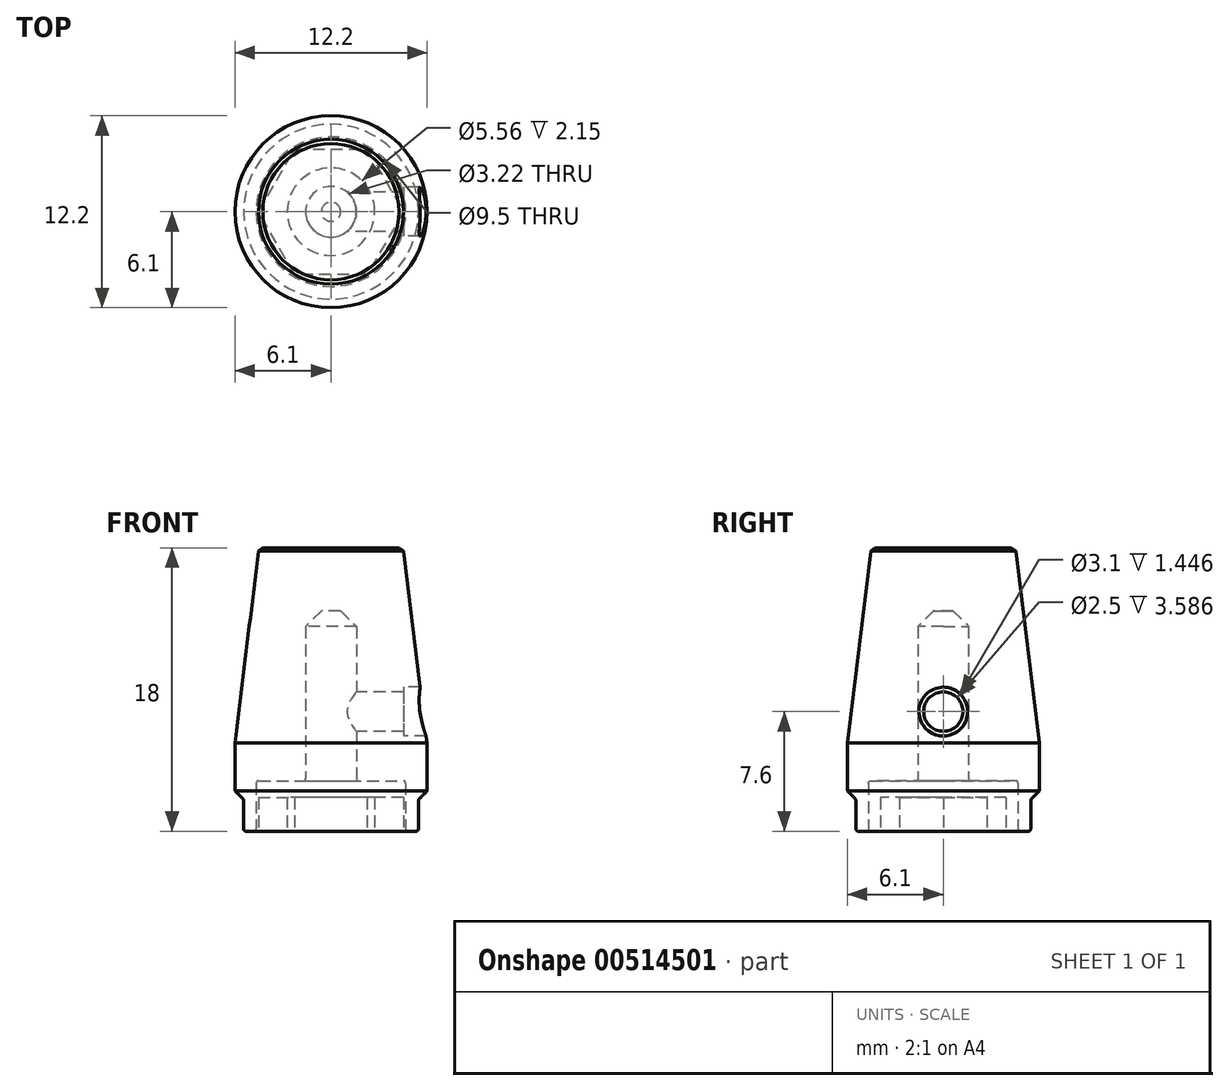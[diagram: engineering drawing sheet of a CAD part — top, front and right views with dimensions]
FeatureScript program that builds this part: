
annotation { "Feature Type Name" : "Feature", "Feature Type Description" : "" }
export const myFeature = defineFeature(function(context is Context, id is Id, definition is map)
    precondition{}
    {
        {
            var Q0;
            Q0=qCreatedBy(makeId("Front.planeOp"),FACE);
            var sketch = newSketch(context, id + "F0", { "sketchPlane" : qUnion([Q0])});
            skLineSegment(sketch, "E0.bottom", {"start": v(4.75, 0) * mm, "end": v(5.55, 0) * mm});
            skLineSegment(sketch, "E0.top", {"start": v(0, 18) * mm, "end": v(4.58, 18) * mm});
            skLineSegment(sketch, "E0.left", {"start": v(0, 3.2) * mm, "end": v(0, 18) * mm, "construction": true});
            skLineSegment(sketch, "E0.right", {"start": v(6.1, 2) * mm, "end": v(6.1, 5.6) * mm});
            skLineSegment(sketch, "E1", {"start": v(1.6, 3.2) * mm, "end": v(4.75, 3.2) * mm});
            skLineSegment(sketch, "E2", {"start": v(4.75, 3.2) * mm, "end": v(4.75, 0) * mm});
            skLineSegment(sketch, "E3", {"start": v(5.55, 0) * mm, "end": v(5.55, 2) * mm});
            skLineSegment(sketch, "E4", {"start": v(5.55, 2) * mm, "end": v(6.1, 2) * mm});
            skLineSegment(sketch, "E5", {"start": v(1.6, 3.2) * mm, "end": v(1.6, 14) * mm});
            skLineSegment(sketch, "E6", {"start": v(1.6, 14) * mm, "end": v(0, 14) * mm});
            skLineSegment(sketch, "E7", {"start": v(0, 18) * mm, "end": v(0, 14) * mm});
            skPoint(sketch, "E8", {"position": v(0, 7.6) * mm});
            skLineSegment(sketch, "E9", {"start": v(4.58, 18) * mm, "end": v(6.1, 5.6) * mm});
            skLineSegment(sketch, "E10", {"start": v(6.1, 5.6) * mm, "end": v(6.1, 20.36) * mm, "construction": true});
            skPoint(sketch, "E11", {"position": v(0, 0) * mm});
            skLineSegment(sketch, "E12", {"start": v(0, 7.6) * mm, "end": v(6.1, 7.6) * mm, "construction": true});
            skPoint(sketch, "E13", {"position": v(6.1, 7.6) * mm});
            skSolve(sketch);
        }
        {
            var Q0;
            Q0=qSketchRegion(id+"F0",true);
            var Q1;
            Q1=sQuery(id+"F0.wireOp",EDGE,"E0.left");
            revolve(context, id + "F1", {"entities" : qUnion([Q0]), "axis" : qUnion([Q1]), "revolveType" : RevolveType.FULL});
        }
        {
            var Q0;
            Q0=makeQuery(id+"F1.opRevolve","SWEPT_EDGE",EDGE,{"disambiguationData":[OSD([sQuery(id+"F0.wireOp",EDGE,"E0.right"),sQuery(id+"F0.wireOp",EDGE,"E4")])]});
            chamfer(context, id + "F2", {"entities" : qUnion([Q0]), "width" : .55 * mm});
        }
        {
            var Q0;
            Q0=makeQuery(id+"F1.opRevolve","SWEPT_EDGE",EDGE,{"disambiguationData":[OSD([sQuery(id+"F0.wireOp",EDGE,"E5"),sQuery(id+"F0.wireOp",EDGE,"E6")])]});
            chamfer(context, id + "F3", {"entities" : qUnion([Q0]), "width" : 1 * mm, "tangentPropagation" : true});
        }
        {
            var Q0;
            Q0=makeQuery(id+"F1.opRevolve","SWEPT_EDGE",EDGE,{"disambiguationData":[OSD([sQuery(id+"F0.wireOp",EDGE,"E0.top"),sQuery(id+"F0.wireOp",EDGE,"E9")])]});
            chamfer(context, id + "F4", {"entities" : qUnion([Q0]), "chamferType" : ChamferType.TWO_OFFSETS, "width1" : .25 * mm, "oppositeDirection" : false, "width2" : .2 * mm, "tangentPropagation" : true});
        }
        {
            var Q0;
            Q0=makeQuery(id+"F1.opRevolve","SWEPT_FACE",FACE,{"disambiguationData":[OSD([sQuery(id+"F0.wireOp",EDGE,"E0.bottom")])]});
            var Q1;
            Q1=makeQuery(id+"F1.opRevolve","SWEPT_EDGE",EDGE,{"disambiguationData":[OSD([sQuery(id+"F0.wireOp",EDGE,"E1"),sQuery(id+"F0.wireOp",EDGE,"E2")])]});
            var Q2;
            Q2=makeQuery(id+"F1.opRevolve","SWEPT_EDGE",EDGE,{"disambiguationData":[OSD([sQuery(id+"F0.wireOp",EDGE,"E1"),sQuery(id+"F0.wireOp",EDGE,"E5")])]});
            var Q3;
            Q3=makeQuery(id+"F2.opChamfer","BLEND_EDGE",EDGE,{"blendedFrom":[makeQuery(id+"F1.opRevolve","SWEPT_EDGE",EDGE,{"disambiguationData":[OSD([sQuery(id+"F0.wireOp",EDGE,"E0.right"),sQuery(id+"F0.wireOp",EDGE,"E4")])]}),makeQuery(id+"F1.opRevolve","SWEPT_FACE",FACE,{"disambiguationData":[OSD([sQuery(id+"F0.wireOp",EDGE,"E3")])]})],"blendedInto":[makeQuery(id+"F1.opRevolve","SWEPT_FACE",FACE,{"disambiguationData":[OSD([sQuery(id+"F0.wireOp",EDGE,"E3")])]})]});
            fillet(context, id + "F5", {"entities" : qUnion([Q0, Q1, Q2, Q3]), "radius" : 0.15 * mm, "tangentPropagation" : true, "allowEdgeOverflow" : false});
        }
        {
            var Q0;
            Q0=sQuery(id+"F0.wireOp",EDGE,"E0.right");
            cPlane(context, id + "F6", {"entities" : qUnion([Q0]), "cplaneType" : CPlaneType.LINE_ANGLE, "offset" : 25 * mm, "angle" : 0 * degree, "width" : 150 * mm, "height" : 150 * mm});
        }
        {
            var Q0;
            Q0=qCreatedBy(id+"F6.planeOp",FACE);
            var sketch = newSketch(context, id + "F7", { "sketchPlane" : qUnion([Q0])});
            skPoint(sketch, "E14.0", {"position": v(0, 7.6) * mm});
            skSolve(sketch);
        }
        {
            var Q0;
            Q0=sQuery(id+"F7.wireOp",VERTEX,"E14.0");
            var Q1;
            Q1=makeQuery(id+"F1.opRevolve","SWEPT_BODY",BODY,{"disambiguationData":[OSD([sQuery(id+"F0.wireOp",EDGE,"E0.bottom"),sQuery(id+"F0.wireOp",EDGE,"E0.top"),sQuery(id+"F0.wireOp",EDGE,"E0.right"),sQuery(id+"F0.wireOp",EDGE,"E1"),sQuery(id+"F0.wireOp",EDGE,"E2"),sQuery(id+"F0.wireOp",EDGE,"E3"),sQuery(id+"F0.wireOp",EDGE,"E4"),sQuery(id+"F0.wireOp",EDGE,"E5"),sQuery(id+"F0.wireOp",EDGE,"E6"),sQuery(id+"F0.wireOp",EDGE,"E7"),sQuery(id+"F0.wireOp",EDGE,"E9")])]});
            hole(context, id + "F8", {"style" : HoleStyle.C_BORE, "endStyle" : HoleEndStyle.BLIND, "holeDiameter" : 2.5 * mm, "cBoreDiameter" : 3.1 * mm, "cBoreDepth" : 1 * mm, "holeDepth" : 5 * mm, "isTappedThrough" : true, "tappedDepth" : 12 * mm, "tapClearance" : 3, "locations" : qUnion([Q0]), "scope" : qUnion([Q1]), "startStyle" : HoleStartStyle.PART});
        }
        {
            var Q0;
            Q0=qCreatedBy(makeId("Top.planeOp"),FACE);
            var sketch = newSketch(context, id + "F9", { "sketchPlane" : qUnion([Q0])});
            skCircle(sketch, "E15.cCircle", {"center": v(0, 0) * mm, "radius": 4 * mm, "construction": true});
            skLineSegment(sketch, "E15.0", {"start": v(2.3, -4) * mm, "end": v(-2.3, -4) * mm});
            skLineSegment(sketch, "E15.1", {"start": v(-2.3, -4) * mm, "end": v(-4.6, 0) * mm});
            skLineSegment(sketch, "E15.2", {"start": v(-4.6, 0) * mm, "end": v(-2.3, 4) * mm});
            skLineSegment(sketch, "E15.3", {"start": v(-2.3, 4) * mm, "end": v(2.3, 4) * mm});
            skLineSegment(sketch, "E15.4", {"start": v(2.3, 4) * mm, "end": v(4.6, 0) * mm});
            skLineSegment(sketch, "E15.5", {"start": v(4.6, 0) * mm, "end": v(2.3, -4) * mm});
            skPoint(sketch, "E15.0.midPoint", {"position": v(0, -4) * mm});
            skCircle(sketch, "E16", {"center": v(0, 0) * mm, "radius": 2.78 * mm});
            skSolve(sketch);
        }
        {
            var Q0;
            Q0 = qSketchRegion(id + "F9", true);
            extrude(context, id + "F10", {"entities" : qUnion([Q0]), "depth" : 2.15 * mm, "offsetDistance" : 25 * mm});
        }
    });
